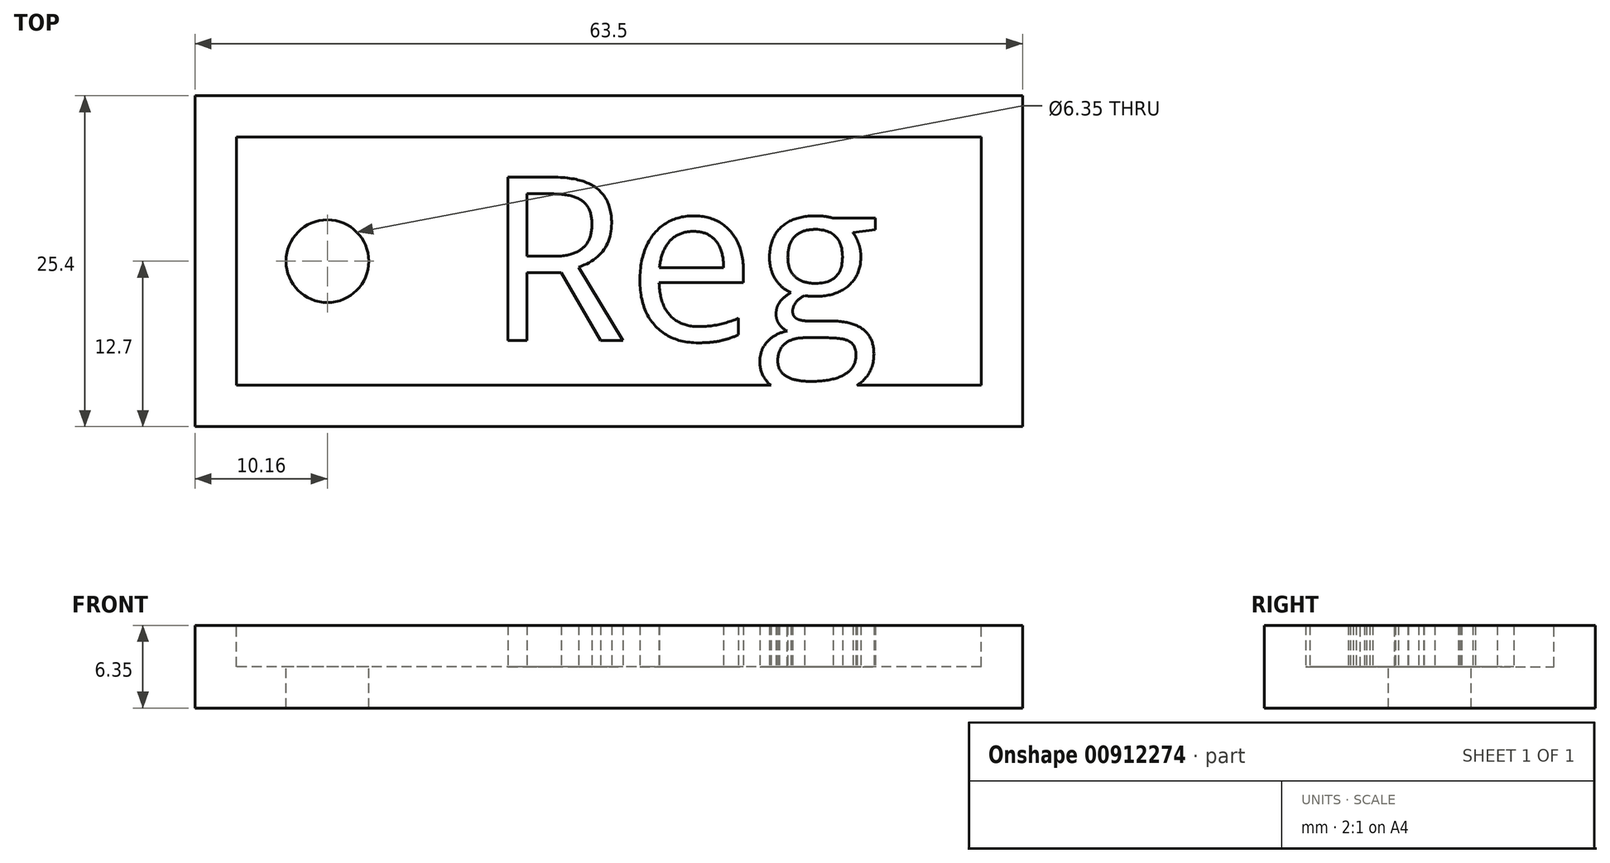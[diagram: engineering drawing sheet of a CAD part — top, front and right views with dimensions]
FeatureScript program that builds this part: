
annotation { "Feature Type Name" : "Feature", "Feature Type Description" : "" }
export const myFeature = defineFeature(function(context is Context, id is Id, definition is map)
    precondition{}
    {
        {
            var Q0;
            Q0=qCreatedBy(makeId("Top.planeOp"),FACE);
            var sketch = newSketch(context, id + "F0", { "sketchPlane" : qUnion([Q0])});
            skLineSegment(sketch, "E0.bottom", {"start": v(31.75, -12.7) * mm, "end": v(-31.75, -12.7) * mm});
            skLineSegment(sketch, "E0.top", {"start": v(31.75, 12.7) * mm, "end": v(-31.75, 12.7) * mm});
            skLineSegment(sketch, "E0.left", {"start": v(31.75, -12.7) * mm, "end": v(31.75, 12.7) * mm});
            skLineSegment(sketch, "E0.right", {"start": v(-31.75, -12.7) * mm, "end": v(-31.75, 12.7) * mm});
            skPoint(sketch, "E0.middle", {"position": v(0, 0) * mm});
            skSolve(sketch);
        }
        {
            var Q0;
            Q0 = qSketchRegion(id + "F0", true);
            extrude(context, id + "F1", {"entities" : qUnion([Q0]), "depth" : 6.35 * mm, "offsetDistance" : 25.4 * mm});
        }
        {
            var Q0;
            Q0=makeQuery(id+"F1.opExtrude","CAP_FACE",FACE,{"disambiguationData":[OSD([sQuery(id+"F0.wireOp",EDGE,"E0.bottom"),sQuery(id+"F0.wireOp",EDGE,"E0.top"),sQuery(id+"F0.wireOp",EDGE,"E0.left"),sQuery(id+"F0.wireOp",EDGE,"E0.right")])],"isStart":false});
            var sketch = newSketch(context, id + "F2", { "sketchPlane" : qUnion([Q0])});
            skLineSegment(sketch, "E1.bottom", {"start": v(28.58, -9.52) * mm, "end": v(-28.58, -9.53) * mm});
            skLineSegment(sketch, "E1.top", {"start": v(28.58, 9.53) * mm, "end": v(-28.58, 9.52) * mm});
            skLineSegment(sketch, "E1.left", {"start": v(28.58, -9.52) * mm, "end": v(28.58, 9.53) * mm});
            skLineSegment(sketch, "E1.right", {"start": v(-28.58, -9.53) * mm, "end": v(-28.58, 9.52) * mm});
            skPoint(sketch, "E1.middle", {"position": v(0, 0) * mm});
            skSolve(sketch);
        }
        {
            var Q0;
            Q0 = qSketchRegion(id + "F2", true);
            extrude(context, id + "F3", {"entities" : qUnion([Q0]), "operationType" : NewBodyOperationType.REMOVE, "oppositeDirection" : true, "depth" : 3.17 * mm, "offsetDistance" : 25.4 * mm});
        }
        {
            var Q0;
            Q0=makeQuery(id+"F3.boolean.opBoolean","COPY",FACE,{"derivedFrom":makeQuery(id+"F3.opExtrude","CAP_FACE",FACE,{"disambiguationData":[OSD([sQuery(id+"F2.wireOp",EDGE,"E1.bottom"),sQuery(id+"F2.wireOp",EDGE,"E1.top"),sQuery(id+"F2.wireOp",EDGE,"E1.left"),sQuery(id+"F2.wireOp",EDGE,"E1.right")])],"isStart":false})});
            var sketch = newSketch(context, id + "F4", { "sketchPlane" : qUnion([Q0])});
            skText(sketch, "E2", { "text": "Reg\n", "fontName": "OpenSans-Regular.ttf"});
            const initialGuessF4  = {"E2": [-0.00946, -0.00609, 1, 0, 0.01265]};
            skSetInitialGuess(sketch, initialGuessF4);
            skSolve(sketch);
        }
        {
            var Q0;
            Q0 = qSketchRegion(id + "F4", true);
            extrude(context, id + "F5", {"entities" : qUnion([Q0]), "operationType" : NewBodyOperationType.ADD, "depth" : 3.17 * mm, "offsetDistance" : 25.4 * mm});
        }
        {
            var Q0;
            {var subQ0=sQuery(id+"F2.wireOp",EDGE,"E1.right");var subQ1=sQuery(id+"F2.wireOp",EDGE,"E1.bottom");var subQ2=sQuery(id+"F2.wireOp",EDGE,"E1.top");var subQ3=sQuery(id+"F2.wireOp",EDGE,"E1.left");Q0=makeQuery(id+"F5.boolean.opBoolean","SPLIT",FACE,{"disambiguationData":[TD([makeQuery(id+"F3.boolean.opBoolean","COPY",FACE,{"derivedFrom":makeQuery(id+"F3.opExtrude","SWEPT_FACE",FACE,{"disambiguationData":[OSD([subQ1])]})})])],"derivedFrom":makeQuery(id+"F3.boolean.opBoolean","COPY",FACE,{"derivedFrom":makeQuery(id+"F3.opExtrude","CAP_FACE",FACE,{"disambiguationData":[OSD([subQ1,subQ2,subQ3,subQ0])],"isStart":false})})});}
            var sketch = newSketch(context, id + "F6", { "sketchPlane" : qUnion([Q0])});
            skCircle(sketch, "E3", {"center": v(-21.59, 0) * mm, "radius": 3.18 * mm});
            skSolve(sketch);
        }
        {
            var Q0;
            Q0 = qSketchRegion(id + "F6", true);
            extrude(context, id + "F7", {"entities" : qUnion([Q0]), "operationType" : NewBodyOperationType.REMOVE, "endBound" : BoundingType.THROUGH_ALL, "oppositeDirection" : true, "depth" : 25.4 * mm, "offsetDistance" : 25.4 * mm});
        }
    });
